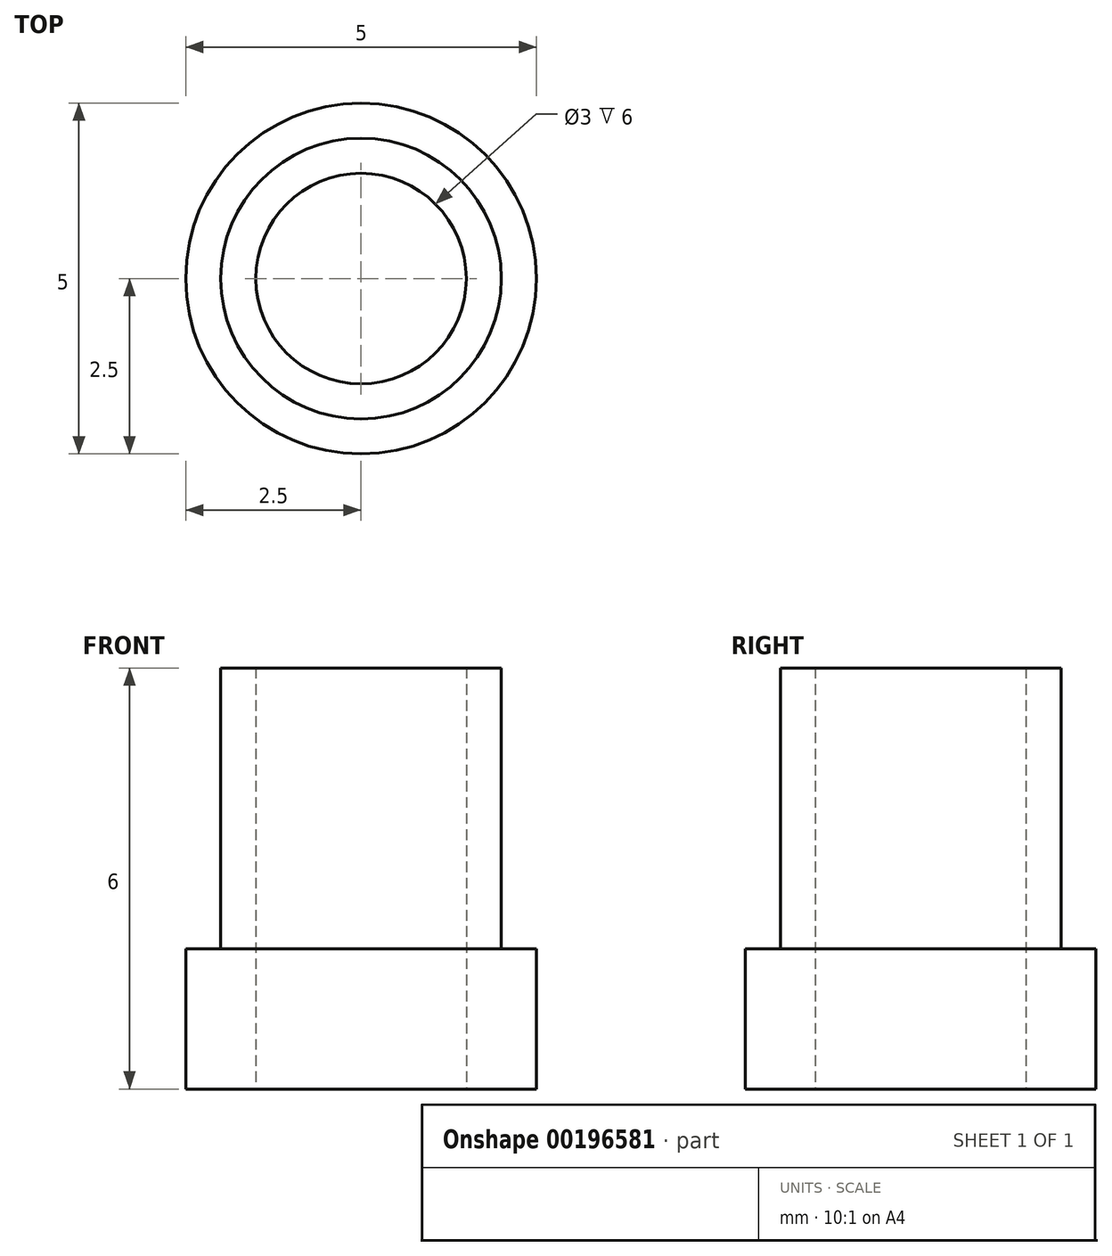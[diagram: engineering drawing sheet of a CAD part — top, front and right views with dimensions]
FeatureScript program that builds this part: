
annotation { "Feature Type Name" : "Feature", "Feature Type Description" : "" }
export const myFeature = defineFeature(function(context is Context, id is Id, definition is map)
    precondition{}
    {
        {
            var Q0;
            Q0=qCreatedBy(makeId("Front.planeOp"),FACE);
            var sketch = newSketch(context, id + "F0", { "sketchPlane" : qUnion([Q0])});
            skLineSegment(sketch, "E0", {"start": v(1.5, 0) * mm, "end": v(2.5, 0) * mm});
            skLineSegment(sketch, "E1", {"start": v(2.5, 0) * mm, "end": v(2.5, 2) * mm});
            skLineSegment(sketch, "E2", {"start": v(2.5, 2) * mm, "end": v(2, 2) * mm});
            skLineSegment(sketch, "E3", {"start": v(2, 2) * mm, "end": v(2, 6) * mm});
            skLineSegment(sketch, "E4", {"start": v(2, 6) * mm, "end": v(1.5, 6) * mm});
            skLineSegment(sketch, "E5", {"start": v(0, 0) * mm, "end": v(0, 9.94) * mm, "construction": true});
            skLineSegment(sketch, "E6", {"start": v(1.5, 6) * mm, "end": v(1.5, 0) * mm});
            skSolve(sketch);
        }
        {
            var Q0;
            Q0 = qSketchRegion(id + "F0", true);
            var Q1;
            Q1=sQuery(id+"F0.wireOp",EDGE,"E5");
            revolve(context, id + "F1", {"entities" : qUnion([Q0]), "axis" : qUnion([Q1]), "revolveType" : RevolveType.FULL});
        }
    });
